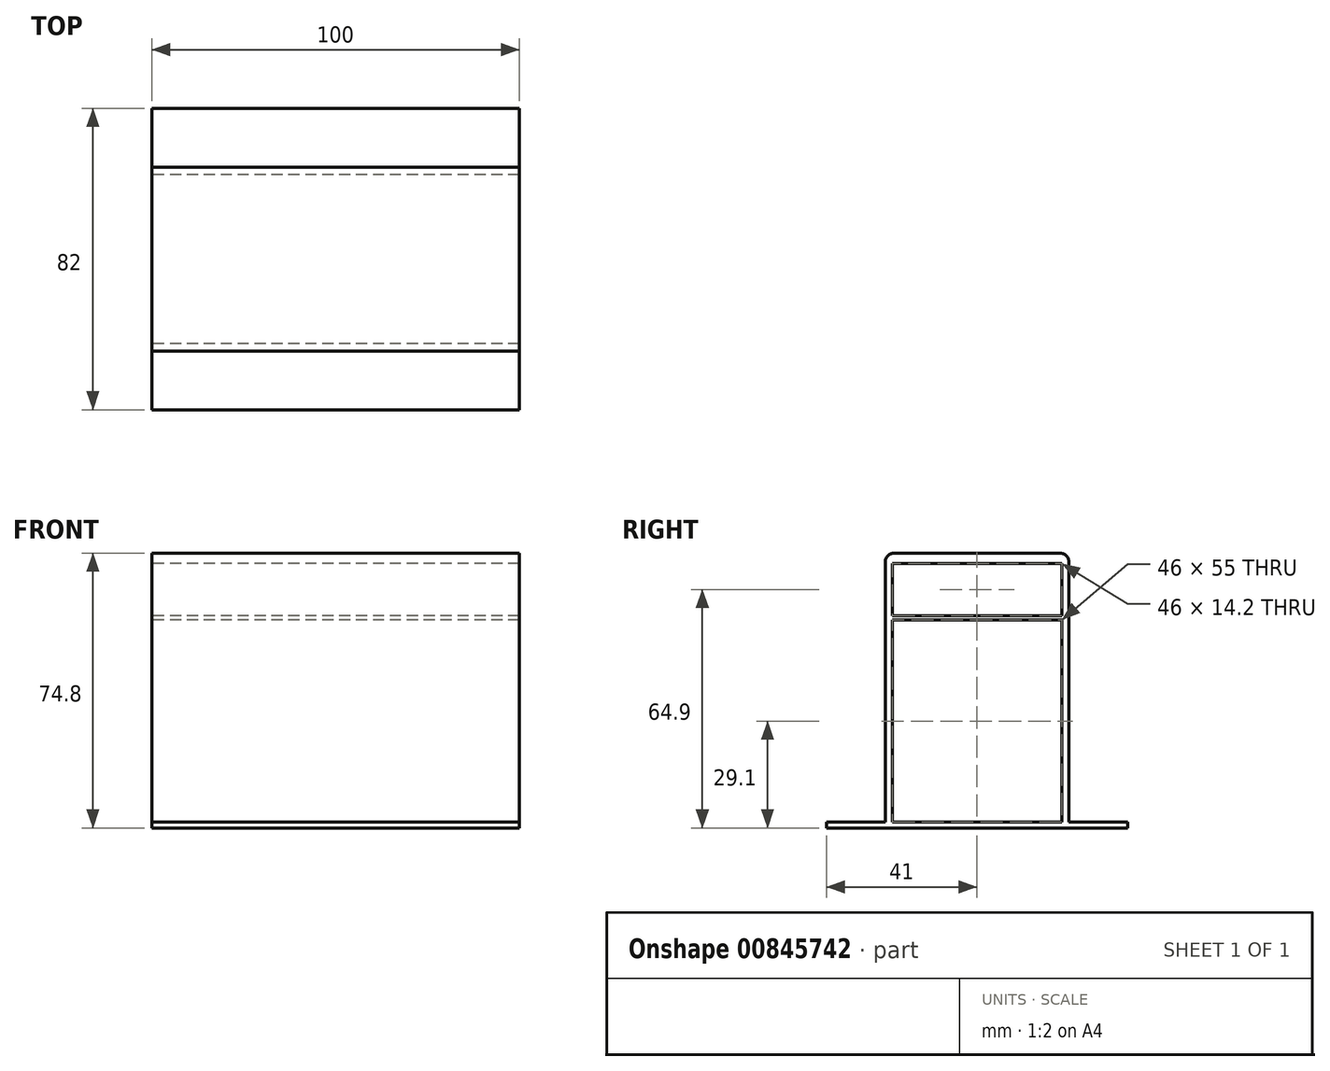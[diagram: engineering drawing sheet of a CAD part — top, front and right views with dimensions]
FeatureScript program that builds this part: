
annotation { "Feature Type Name" : "Feature", "Feature Type Description" : "" }
export const myFeature = defineFeature(function(context is Context, id is Id, definition is map)
    precondition{}
    {
        {
            var Q0;
            Q0=qCreatedBy(makeId("Right.planeOp"),FACE);
            var sketch = newSketch(context, id + "F0", { "sketchPlane" : qUnion([Q0])});
            skLineSegment(sketch, "E0", {"start": v(0, 0) * mm, "end": v(-41, 0) * mm});
            skLineSegment(sketch, "E1", {"start": v(-41, 0) * mm, "end": v(-41, 1.6) * mm});
            skLineSegment(sketch, "E2", {"start": v(-41, 1.6) * mm, "end": v(-25, 1.6) * mm});
            skLineSegment(sketch, "E3", {"start": v(-25, 1.6) * mm, "end": v(-25, 74.8) * mm});
            skLineSegment(sketch, "E4", {"start": v(-25, 74.8) * mm, "end": v(0, 74.8) * mm});
            skLineSegment(sketch, "E5", {"start": v(0, 74.8) * mm, "end": v(0, 72) * mm});
            skLineSegment(sketch, "E6", {"start": v(0, 72) * mm, "end": v(-23, 72) * mm});
            skLineSegment(sketch, "E7", {"start": v(-23, 72) * mm, "end": v(-23, 57.8) * mm});
            skLineSegment(sketch, "E8", {"start": v(-23, 57.8) * mm, "end": v(0, 57.8) * mm});
            skLineSegment(sketch, "E9", {"start": v(0, 57.8) * mm, "end": v(0, 56.6) * mm});
            skLineSegment(sketch, "E10", {"start": v(0, 56.6) * mm, "end": v(-23, 56.6) * mm});
            skLineSegment(sketch, "E11", {"start": v(-23, 56.6) * mm, "end": v(-23, 1.6) * mm});
            skLineSegment(sketch, "E12", {"start": v(-23, 1.6) * mm, "end": v(0, 1.6) * mm});
            skLineSegment(sketch, "E13", {"start": v(0, 1.6) * mm, "end": v(0, 0) * mm});
            skSolve(sketch);
        }
        {
            var Q0;
            Q0 = qSketchRegion(id + "F0", true);
            extrude(context, id + "F1", {"entities" : qUnion([Q0]), "depth" : 100 * mm, "offsetDistance" : 25 * mm});
        }
        {
            var Q0;
            Q0=makeQuery(id+"F1.opExtrude","SWEPT_BODY",BODY,{"disambiguationData":[OSD([sQuery(id+"F0.wireOp",EDGE,"E0"),sQuery(id+"F0.wireOp",EDGE,"E1"),sQuery(id+"F0.wireOp",EDGE,"E2"),sQuery(id+"F0.wireOp",EDGE,"E3"),sQuery(id+"F0.wireOp",EDGE,"E4"),sQuery(id+"F0.wireOp",EDGE,"E5"),sQuery(id+"F0.wireOp",EDGE,"E6"),sQuery(id+"F0.wireOp",EDGE,"E7"),sQuery(id+"F0.wireOp",EDGE,"E8"),sQuery(id+"F0.wireOp",EDGE,"E9"),sQuery(id+"F0.wireOp",EDGE,"E10"),sQuery(id+"F0.wireOp",EDGE,"E11"),sQuery(id+"F0.wireOp",EDGE,"E12"),sQuery(id+"F0.wireOp",EDGE,"E13")])]});
            var Q1;
            Q1=qCreatedBy(makeId("Front.planeOp"),FACE);
            mirror(context, id + "F2", {"operationType" : NewBodyOperationType.ADD, "entities" : qUnion([Q0]), "mirrorPlane" : qUnion([Q1])});
        }
        {
            var Q0;
            Q0=makeQuery(id+"F1.opExtrude","SWEPT_EDGE",EDGE,{"disambiguationData":[OSD([sQuery(id+"F0.wireOp",EDGE,"E3"),sQuery(id+"F0.wireOp",EDGE,"E4")])]});
            var Q1;
            Q1=makeQuery(id+"F2.opPattern","COPY",EDGE,{"derivedFrom":makeQuery(id+"F1.opExtrude","SWEPT_EDGE",EDGE,{"disambiguationData":[OSD([sQuery(id+"F0.wireOp",EDGE,"E3"),sQuery(id+"F0.wireOp",EDGE,"E4")])]}),"instanceName":"1"});
            fillet(context, id + "F3", {"entities" : qUnion([Q0, Q1]), "radius" : 2.5 * mm, "tangentPropagation" : true, "allowEdgeOverflow" : false});
        }
    });
